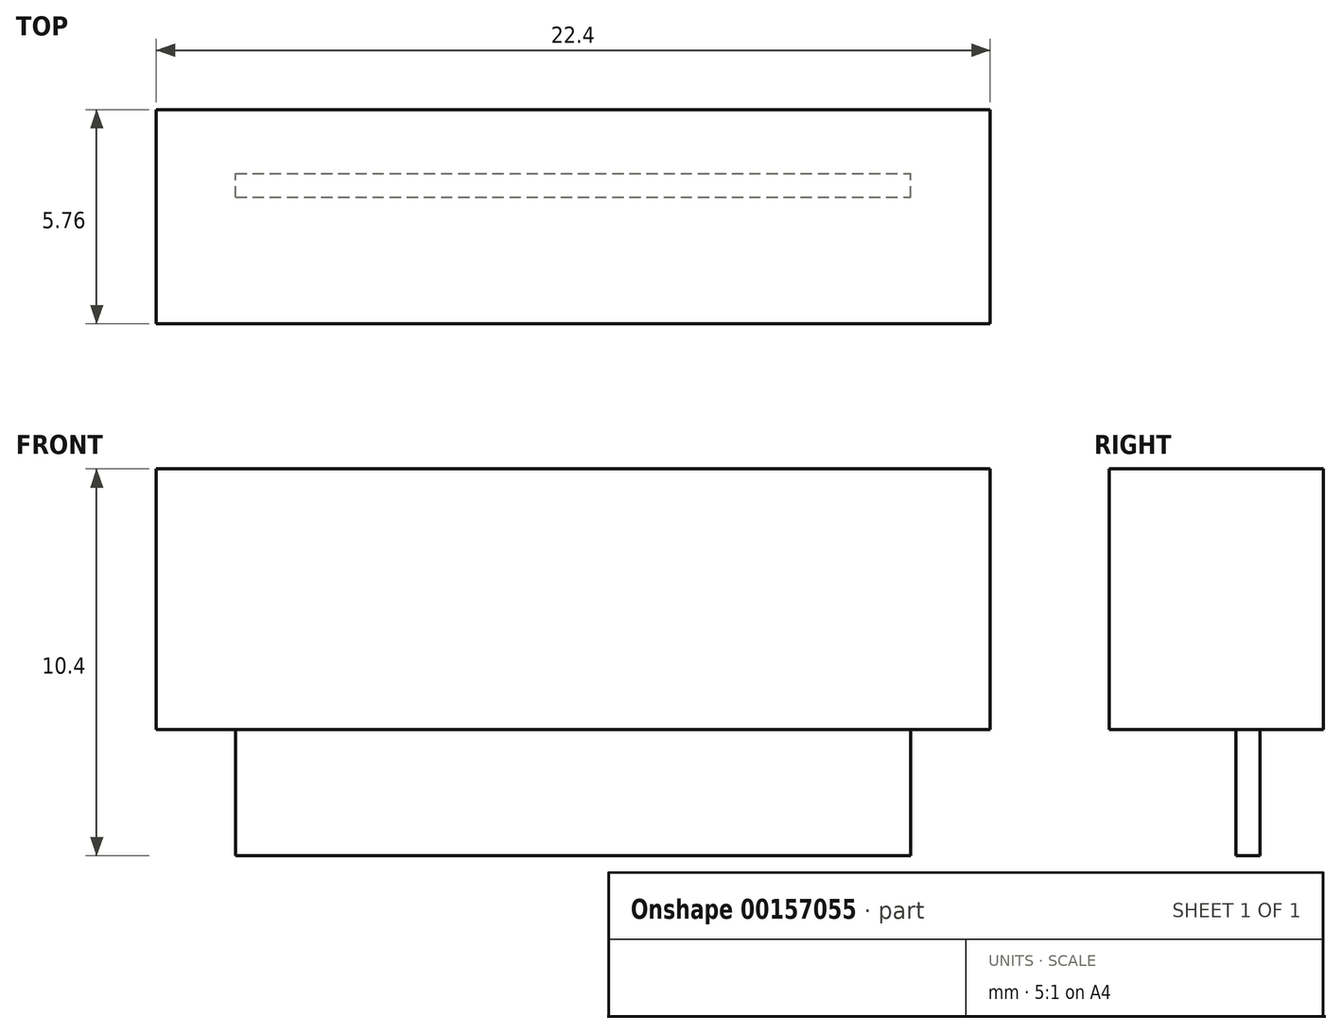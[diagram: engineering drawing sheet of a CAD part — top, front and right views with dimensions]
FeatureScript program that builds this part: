
annotation { "Feature Type Name" : "Feature", "Feature Type Description" : "" }
export const myFeature = defineFeature(function(context is Context, id is Id, definition is map)
    precondition{}
    {
        {
            var Q0;
            Q0=qCreatedBy(makeId("Top.planeOp"),FACE);
            var sketch = newSketch(context, id + "F0", { "sketchPlane" : qUnion([Q0])});
            skLineSegment(sketch, "E0.bottom", {"start": v(11.2, 2.88) * mm, "end": v(-11.2, 2.88) * mm});
            skLineSegment(sketch, "E0.top", {"start": v(11.2, -2.88) * mm, "end": v(-11.2, -2.88) * mm});
            skLineSegment(sketch, "E0.left", {"start": v(11.2, 2.88) * mm, "end": v(11.2, -2.88) * mm});
            skLineSegment(sketch, "E0.right", {"start": v(-11.2, 2.88) * mm, "end": v(-11.2, -2.88) * mm});
            skPoint(sketch, "E0.middle", {"position": v(0, 0) * mm});
            skSolve(sketch);
        }
        {
            var Q0;
            Q0=makeQuery(id+"F0.imprint","IMPRINT",FACE,{"disambiguationData":[TD([[makeQuery(id+"F0.imprint","IMPRINT",EDGE,{"derivedFrom":sQuery(id+"F0.wireOp",EDGE,"E0.bottom")}),1.0]])]});
            extrude(context, id + "F1", {"entities" : qUnion([Q0]), "depth" : 7 * mm});
        }
        {
            var Q0;
            Q0=makeQuery(id+"F1.opExtrude","CAP_FACE",FACE,{"disambiguationData":[OSD([sQuery(id+"F0.wireOp",EDGE,"E0.bottom"),sQuery(id+"F0.wireOp",EDGE,"E0.top"),sQuery(id+"F0.wireOp",EDGE,"E0.left"),sQuery(id+"F0.wireOp",EDGE,"E0.right")])],"isStart":true});
            var sketch = newSketch(context, id + "F2", { "sketchPlane" : qUnion([Q0])});
            skPoint(sketch, "E1.middle", {"position": v(0, 0) * mm});
            skLineSegment(sketch, "E2.bottom", {"start": v(-9.07, -0.53) * mm, "end": v(9.07, -0.53) * mm});
            skLineSegment(sketch, "E2.top", {"start": v(-9.07, -1.17) * mm, "end": v(9.07, -1.17) * mm});
            skLineSegment(sketch, "E2.left", {"start": v(-9.07, -0.53) * mm, "end": v(-9.07, -1.17) * mm});
            skLineSegment(sketch, "E2.right", {"start": v(9.07, -0.53) * mm, "end": v(9.07, -1.17) * mm});
            skLineSegment(sketch, "E3", {"start": v(-9.07, -1.17) * mm, "end": v(-11.2, -1.17) * mm, "construction": true});
            skLineSegment(sketch, "E4", {"start": v(9.07, -1.17) * mm, "end": v(11.2, -1.17) * mm, "construction": true});
            skSolve(sketch);
        }
        {
            var Q0;
            Q0=qSketchRegion(id+"F2",true);
            extrude(context, id + "F3", {"entities" : qUnion([Q0]), "operationType" : NewBodyOperationType.ADD, "depth" : 3.4 * mm});
        }
    });
